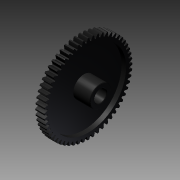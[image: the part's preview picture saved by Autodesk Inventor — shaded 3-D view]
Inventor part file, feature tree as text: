
AUTODESK INVENTOR PART (.ipt)
format: ipt  version: 2012 (Build 160160000, 160)  size: 999,424 bytes
history: native  units: in
note: dims shown in document units (in); Inventor stores cm internally (conversion verified against a paired STEP export)
features: sketch x1, imported_body x1
ambient origin geometry x8: Origin, YZ Plane, XZ Plane, XY Plane, X Axis, Y Axis, Z Axis, Center Point
feature tree (2):
  sketch  "Sketch1"  dims[d0=2.3in]
  imported_body  "Base1"
